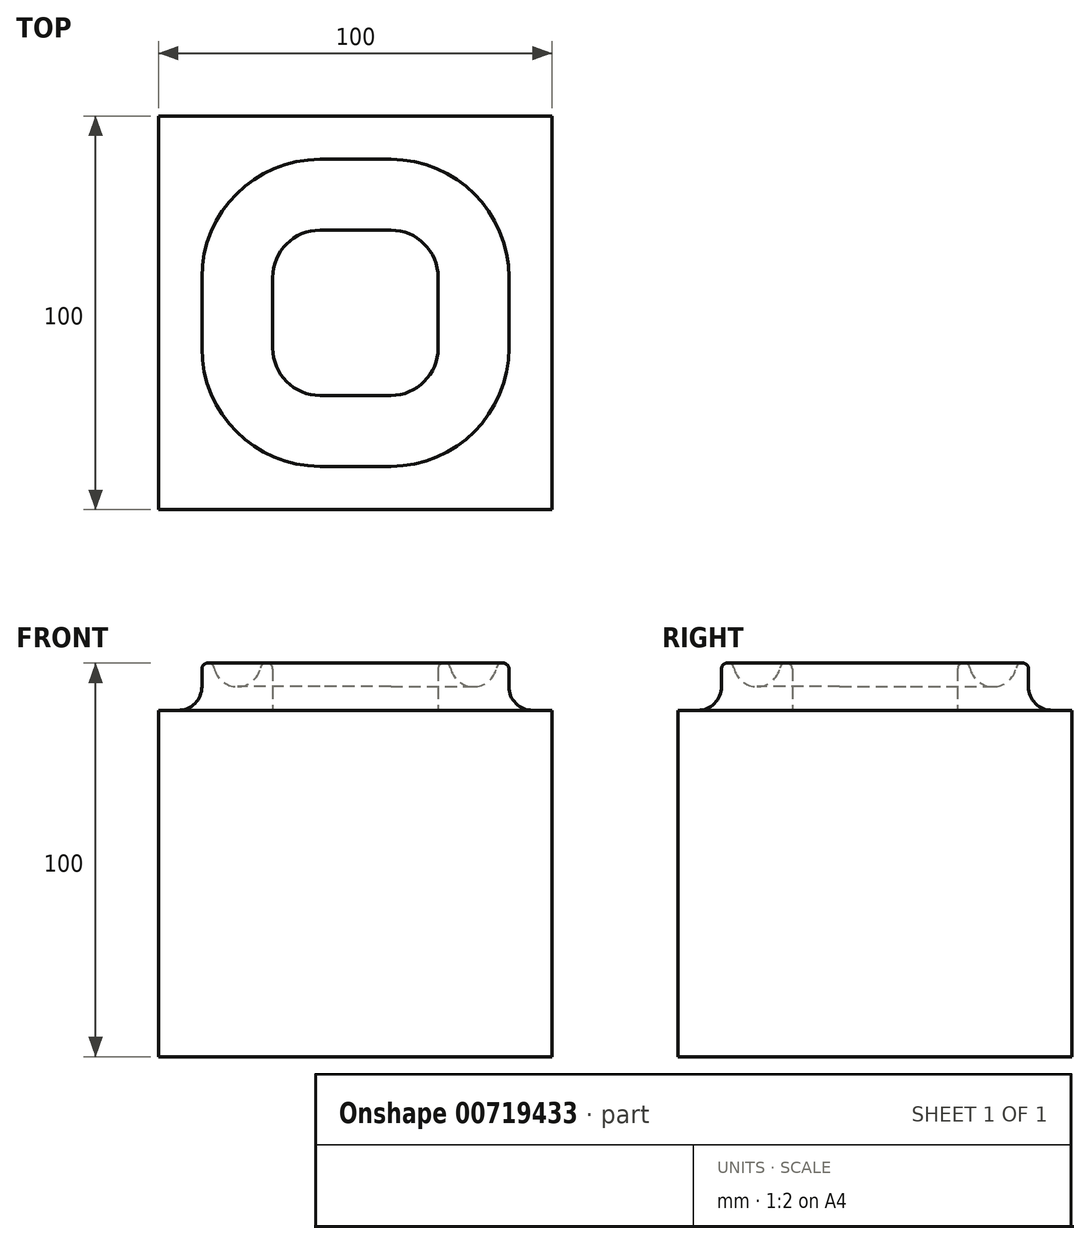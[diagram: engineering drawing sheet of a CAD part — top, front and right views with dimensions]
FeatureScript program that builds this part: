
annotation { "Feature Type Name" : "Feature", "Feature Type Description" : "" }
export const myFeature = defineFeature(function(context is Context, id is Id, definition is map)
    precondition{}
    {
        {
            var Q0;
            Q0=qCreatedBy(makeId("Top.planeOp"),FACE);
            var sketch = newSketch(context, id + "F0", { "sketchPlane" : qUnion([Q0])});
            skLineSegment(sketch, "E0.bottom", {"start": v(50, 50) * mm, "end": v(-50, 50) * mm});
            skLineSegment(sketch, "E0.top", {"start": v(50, -50) * mm, "end": v(-50, -50) * mm});
            skLineSegment(sketch, "E0.left", {"start": v(50, 50) * mm, "end": v(50, -50) * mm});
            skLineSegment(sketch, "E0.right", {"start": v(-50, 50) * mm, "end": v(-50, -50) * mm});
            skPoint(sketch, "E0.middle", {"position": v(0, 0) * mm});
            skLineSegment(sketch, "E1.bottom", {"start": v(9, 15) * mm, "end": v(-9, 15) * mm, "construction": true});
            skLineSegment(sketch, "E1.top", {"start": v(9, -15) * mm, "end": v(-9, -15) * mm, "construction": true});
            skLineSegment(sketch, "E1.left", {"start": v(15, 9) * mm, "end": v(15, -9) * mm, "construction": true});
            skLineSegment(sketch, "E1.right", {"start": v(-15, 9) * mm, "end": v(-15, -9) * mm, "construction": true});
            skPoint(sketch, "E2.visualSharp", {"position": v(-15, 15) * mm});
            skArc(sketch, "E2.filletArc", {"start": v(-9, 15) * mm, "mid": v(-13.24, 13.24) * mm, "end": v(-15, 9) * mm, "construction": true});
            skPoint(sketch, "E3.visualSharp", {"position": v(15, 15) * mm});
            skArc(sketch, "E3.filletArc", {"start": v(15, 9) * mm, "mid": v(13.24, 13.24) * mm, "end": v(9, 15) * mm, "construction": true});
            skPoint(sketch, "E4.visualSharp", {"position": v(15, -15) * mm});
            skArc(sketch, "E4.filletArc", {"start": v(9, -15) * mm, "mid": v(13.24, -13.24) * mm, "end": v(15, -9) * mm, "construction": true});
            skPoint(sketch, "E5.visualSharp", {"position": v(-15, -15) * mm});
            skArc(sketch, "E5.filletArc", {"start": v(-15, -9) * mm, "mid": v(-13.24, -13.24) * mm, "end": v(-9, -15) * mm, "construction": true});
            skArc(sketch, "E6.0", {"start": v(45, 9) * mm, "mid": v(34.46, 34.46) * mm, "end": v(9, 45) * mm, "construction": true});
            skLineSegment(sketch, "E6.1", {"start": v(45, 9) * mm, "end": v(45, -9) * mm, "construction": true});
            skLineSegment(sketch, "E6.2", {"start": v(9, 45) * mm, "end": v(-9, 45) * mm, "construction": true});
            skArc(sketch, "E6.3", {"start": v(9, -45) * mm, "mid": v(34.46, -34.46) * mm, "end": v(45, -9) * mm, "construction": true});
            skArc(sketch, "E6.4", {"start": v(-9, 45) * mm, "mid": v(-34.46, 34.46) * mm, "end": v(-45, 9) * mm, "construction": true});
            skLineSegment(sketch, "E6.5", {"start": v(-45, 9) * mm, "end": v(-45, -9) * mm, "construction": true});
            skArc(sketch, "E6.6", {"start": v(-45, -9) * mm, "mid": v(-34.46, -34.46) * mm, "end": v(-9, -45) * mm, "construction": true});
            skLineSegment(sketch, "E6.7", {"start": v(9, -45) * mm, "end": v(-9, -45) * mm, "construction": true});
            skArc(sketch, "E7.0", {"start": v(21, 9) * mm, "mid": v(17.49, 17.49) * mm, "end": v(9, 21) * mm});
            skLineSegment(sketch, "E7.1", {"start": v(21, 9) * mm, "end": v(21, -9) * mm});
            skLineSegment(sketch, "E7.2", {"start": v(9, 21) * mm, "end": v(-9, 21) * mm});
            skArc(sketch, "E7.3", {"start": v(9, -21) * mm, "mid": v(17.49, -17.49) * mm, "end": v(21, -9) * mm});
            skArc(sketch, "E7.4", {"start": v(-9, 21) * mm, "mid": v(-17.49, 17.49) * mm, "end": v(-21, 9) * mm});
            skLineSegment(sketch, "E7.5", {"start": v(-21, 9) * mm, "end": v(-21, -9) * mm});
            skArc(sketch, "E7.6", {"start": v(-21, -9) * mm, "mid": v(-17.49, -17.49) * mm, "end": v(-9, -21) * mm});
            skLineSegment(sketch, "E7.7", {"start": v(9, -21) * mm, "end": v(-9, -21) * mm});
            skArc(sketch, "E8.0", {"start": v(39, 9) * mm, "mid": v(30.21, 30.21) * mm, "end": v(9, 39) * mm});
            skLineSegment(sketch, "E8.1", {"start": v(39, 9) * mm, "end": v(39, -9) * mm});
            skLineSegment(sketch, "E8.2", {"start": v(9, 39) * mm, "end": v(-9, 39) * mm});
            skArc(sketch, "E8.3", {"start": v(9, -39) * mm, "mid": v(30.21, -30.21) * mm, "end": v(39, -9) * mm});
            skArc(sketch, "E8.4", {"start": v(-9, 39) * mm, "mid": v(-30.21, 30.21) * mm, "end": v(-39, 9) * mm});
            skLineSegment(sketch, "E8.5", {"start": v(-39, 9) * mm, "end": v(-39, -9) * mm});
            skArc(sketch, "E8.6", {"start": v(-39, -9) * mm, "mid": v(-30.21, -30.21) * mm, "end": v(-9, -39) * mm});
            skLineSegment(sketch, "E8.7", {"start": v(9, -39) * mm, "end": v(-9, -39) * mm});
            skArc(sketch, "E9.0", {"start": v(24, 9) * mm, "mid": v(19.6, 19.6) * mm, "end": v(9, 24) * mm});
            skLineSegment(sketch, "E9.1", {"start": v(24, 9) * mm, "end": v(24, -9) * mm});
            skLineSegment(sketch, "E9.2", {"start": v(9, 24) * mm, "end": v(-9, 24) * mm});
            skArc(sketch, "E9.3", {"start": v(9, -24) * mm, "mid": v(19.6, -19.6) * mm, "end": v(24, -9) * mm});
            skArc(sketch, "E9.4", {"start": v(-9, 24) * mm, "mid": v(-19.6, 19.6) * mm, "end": v(-24, 9) * mm});
            skLineSegment(sketch, "E9.5", {"start": v(-24, 9) * mm, "end": v(-24, -9) * mm});
            skArc(sketch, "E9.6", {"start": v(-24, -9) * mm, "mid": v(-19.6, -19.6) * mm, "end": v(-9, -24) * mm});
            skLineSegment(sketch, "E9.7", {"start": v(9, -24) * mm, "end": v(-9, -24) * mm});
            skLineSegment(sketch, "E10.0", {"start": v(9, 36) * mm, "end": v(-9, 36) * mm});
            skArc(sketch, "E10.1", {"start": v(36, 9) * mm, "mid": v(28.1, 28.1) * mm, "end": v(9, 36) * mm});
            skArc(sketch, "E10.2", {"start": v(-9, 36) * mm, "mid": v(-28.1, 28.1) * mm, "end": v(-36, 9) * mm});
            skLineSegment(sketch, "E10.3", {"start": v(36, 9) * mm, "end": v(36, -9) * mm});
            skLineSegment(sketch, "E10.4", {"start": v(-36, 9) * mm, "end": v(-36, -9) * mm});
            skArc(sketch, "E10.5", {"start": v(-36, -9) * mm, "mid": v(-28.1, -28.1) * mm, "end": v(-9, -36) * mm});
            skLineSegment(sketch, "E10.6", {"start": v(9, -36) * mm, "end": v(-9, -36) * mm});
            skArc(sketch, "E10.7", {"start": v(9, -36) * mm, "mid": v(28.1, -28.1) * mm, "end": v(36, -9) * mm});
            skSolve(sketch);
        }
        {
            var Q0;
            Q0=makeQuery(id+"F0.imprint","IMPRINT",FACE,{"disambiguationData":[TD([[makeQuery(id+"F0.imprint","IMPRINT",EDGE,{"derivedFrom":sQuery(id+"F0.wireOp",EDGE,"E0.bottom")}),1.0]])]});
            var Q1;
            Q1=makeQuery(id+"F0.imprint","IMPRINT",FACE,{"disambiguationData":[TD([[makeQuery(id+"F0.imprint","IMPRINT",EDGE,{"derivedFrom":sQuery(id+"F0.wireOp",EDGE,"E9.0")}),-1.0]])]});
            var Q2;
            Q2=makeQuery(id+"F0.imprint","IMPRINT",FACE,{"disambiguationData":[TD([[makeQuery(id+"F0.imprint","IMPRINT",EDGE,{"derivedFrom":sQuery(id+"F0.wireOp",EDGE,"E8.0")}),1.0]])]});
            var Q3;
            Q3=makeQuery(id+"F0.imprint","IMPRINT",FACE,{"disambiguationData":[TD([[makeQuery(id+"F0.imprint","IMPRINT",EDGE,{"derivedFrom":sQuery(id+"F0.wireOp",EDGE,"E7.0")}),-1.0]])]});
            var Q4;
            Q4=makeQuery(id+"F0.imprint","IMPRINT",FACE,{"disambiguationData":[TD([[makeQuery(id+"F0.imprint","IMPRINT",EDGE,{"derivedFrom":sQuery(id+"F0.wireOp",EDGE,"E7.0")}),1.0]])]});
            extrude(context, id + "F1", {"entities" : qUnion([Q0, Q1, Q2, Q3, Q4]), "oppositeDirection" : true, "depth" : 88 * mm, "offsetDistance" : 25 * mm});
        }
        {
            var Q0;
            Q0=makeQuery(id+"F0.imprint","IMPRINT",FACE,{"disambiguationData":[TD([[makeQuery(id+"F0.imprint","IMPRINT",EDGE,{"derivedFrom":sQuery(id+"F0.wireOp",EDGE,"E8.0")}),1.0]])]});
            var Q1;
            Q1=makeQuery(id+"F0.imprint","IMPRINT",FACE,{"disambiguationData":[TD([[makeQuery(id+"F0.imprint","IMPRINT",EDGE,{"derivedFrom":sQuery(id+"F0.wireOp",EDGE,"E9.0")}),-1.0]])]});
            var Q2;
            Q2=makeQuery(id+"F0.imprint","IMPRINT",FACE,{"disambiguationData":[TD([[makeQuery(id+"F0.imprint","IMPRINT",EDGE,{"derivedFrom":sQuery(id+"F0.wireOp",EDGE,"E7.0")}),-1.0]])]});
            extrude(context, id + "F2", {"entities" : qUnion([Q0, Q1, Q2]), "operationType" : NewBodyOperationType.ADD, "depth" : 6 * mm, "offsetDistance" : 25 * mm});
        }
        {
            var Q0;
            Q0=makeQuery(id+"F0.imprint","IMPRINT",FACE,{"disambiguationData":[TD([[makeQuery(id+"F0.imprint","IMPRINT",EDGE,{"derivedFrom":sQuery(id+"F0.wireOp",EDGE,"E8.0")}),1.0]])]});
            var Q1;
            Q1=makeQuery(id+"F0.imprint","IMPRINT",FACE,{"disambiguationData":[TD([[makeQuery(id+"F0.imprint","IMPRINT",EDGE,{"derivedFrom":sQuery(id+"F0.wireOp",EDGE,"E7.0")}),-1.0]])]});
            extrude(context, id + "F3", {"entities" : qUnion([Q0, Q1]), "operationType" : NewBodyOperationType.ADD, "depth" : 12 * mm, "offsetDistance" : 25 * mm});
        }
        {
            var Q0;
            Q0=makeQuery(id+"F2.opExtrude","CAP_EDGE",EDGE,{"disambiguationData":[OSD([sQuery(id+"F0.wireOp",EDGE,"E8.5")])],"isStart":true});
            var Q1;
            Q1=makeQuery(id+"F2.opExtrude","CAP_EDGE",EDGE,{"disambiguationData":[OSD([sQuery(id+"F0.wireOp",EDGE,"E7.4")])],"isStart":true});
            var Q2;
            Q2=makeQuery(id+"F3.boolean.opBoolean","INTERSECT",EDGE,{"derivedFrom":[makeQuery(id+"F2.opExtrude","CAP_FACE",FACE,{"disambiguationData":[OSD([sQuery(id+"F0.wireOp",EDGE,"E7.0"),sQuery(id+"F0.wireOp",EDGE,"E7.1"),sQuery(id+"F0.wireOp",EDGE,"E7.2"),sQuery(id+"F0.wireOp",EDGE,"E7.3"),sQuery(id+"F0.wireOp",EDGE,"E7.4"),sQuery(id+"F0.wireOp",EDGE,"E7.5"),sQuery(id+"F0.wireOp",EDGE,"E7.6"),sQuery(id+"F0.wireOp",EDGE,"E7.7"),sQuery(id+"F0.wireOp",EDGE,"E8.0"),sQuery(id+"F0.wireOp",EDGE,"E8.1"),sQuery(id+"F0.wireOp",EDGE,"E8.2"),sQuery(id+"F0.wireOp",EDGE,"E8.3"),sQuery(id+"F0.wireOp",EDGE,"E8.4"),sQuery(id+"F0.wireOp",EDGE,"E8.5"),sQuery(id+"F0.wireOp",EDGE,"E8.6"),sQuery(id+"F0.wireOp",EDGE,"E8.7")])],"isStart":false}),makeQuery(id+"F3.opExtrude","SWEPT_FACE",FACE,{"disambiguationData":[OSD([sQuery(id+"F0.wireOp",EDGE,"E10.2")])]})]});
            var Q3;
            Q3=makeQuery(id+"F3.boolean.opBoolean","INTERSECT",EDGE,{"derivedFrom":[makeQuery(id+"F2.opExtrude","CAP_FACE",FACE,{"disambiguationData":[OSD([sQuery(id+"F0.wireOp",EDGE,"E7.0"),sQuery(id+"F0.wireOp",EDGE,"E7.1"),sQuery(id+"F0.wireOp",EDGE,"E7.2"),sQuery(id+"F0.wireOp",EDGE,"E7.3"),sQuery(id+"F0.wireOp",EDGE,"E7.4"),sQuery(id+"F0.wireOp",EDGE,"E7.5"),sQuery(id+"F0.wireOp",EDGE,"E7.6"),sQuery(id+"F0.wireOp",EDGE,"E7.7"),sQuery(id+"F0.wireOp",EDGE,"E8.0"),sQuery(id+"F0.wireOp",EDGE,"E8.1"),sQuery(id+"F0.wireOp",EDGE,"E8.2"),sQuery(id+"F0.wireOp",EDGE,"E8.3"),sQuery(id+"F0.wireOp",EDGE,"E8.4"),sQuery(id+"F0.wireOp",EDGE,"E8.5"),sQuery(id+"F0.wireOp",EDGE,"E8.6"),sQuery(id+"F0.wireOp",EDGE,"E8.7")])],"isStart":false}),makeQuery(id+"F3.opExtrude","SWEPT_FACE",FACE,{"disambiguationData":[OSD([sQuery(id+"F0.wireOp",EDGE,"E9.5")])]})]});
            fillet(context, id + "F4", {"entities" : qUnion([Q0, Q1, Q2, Q3]), "radius" : 6 * mm, "tangentPropagation" : true, "allowEdgeOverflow" : false});
        }
        {
            var Q0;
            {var subQ0=sQuery(id+"F0.wireOp",EDGE,"E10.2");var subQ1=sQuery(id+"F0.wireOp",EDGE,"E8.7");var subQ2=sQuery(id+"F0.wireOp",EDGE,"E8.6");var subQ3=sQuery(id+"F0.wireOp",EDGE,"E8.5");var subQ4=sQuery(id+"F0.wireOp",EDGE,"E8.4");var subQ5=sQuery(id+"F0.wireOp",EDGE,"E8.3");var subQ6=sQuery(id+"F0.wireOp",EDGE,"E8.2");var subQ7=sQuery(id+"F0.wireOp",EDGE,"E8.1");var subQ8=sQuery(id+"F0.wireOp",EDGE,"E8.0");Q0=makeQuery(id+"F4.opFillet","BLEND_EDGE",EDGE,{"blendedFrom":[makeQuery(id+"F3.boolean.opBoolean","INTERSECT",EDGE,{"derivedFrom":[makeQuery(id+"F2.opExtrude","CAP_FACE",FACE,{"disambiguationData":[OSD([sQuery(id+"F0.wireOp",EDGE,"E7.0"),sQuery(id+"F0.wireOp",EDGE,"E7.1"),sQuery(id+"F0.wireOp",EDGE,"E7.2"),sQuery(id+"F0.wireOp",EDGE,"E7.3"),sQuery(id+"F0.wireOp",EDGE,"E7.4"),sQuery(id+"F0.wireOp",EDGE,"E7.5"),sQuery(id+"F0.wireOp",EDGE,"E7.6"),sQuery(id+"F0.wireOp",EDGE,"E7.7"),subQ8,subQ7,subQ6,subQ5,subQ4,subQ3,subQ2,subQ1])],"isStart":false}),makeQuery(id+"F3.opExtrude","SWEPT_FACE",FACE,{"disambiguationData":[OSD([subQ0])]})]}),makeQuery(id+"F3.opExtrude","CAP_FACE",FACE,{"disambiguationData":[OSD([subQ8,subQ7,subQ6,subQ5,subQ4,subQ3,subQ2,subQ1,sQuery(id+"F0.wireOp",EDGE,"E10.0"),sQuery(id+"F0.wireOp",EDGE,"E10.1"),subQ0,sQuery(id+"F0.wireOp",EDGE,"E10.3"),sQuery(id+"F0.wireOp",EDGE,"E10.4"),sQuery(id+"F0.wireOp",EDGE,"E10.5"),sQuery(id+"F0.wireOp",EDGE,"E10.6"),sQuery(id+"F0.wireOp",EDGE,"E10.7")])],"isStart":false})],"blendedInto":[makeQuery(id+"F3.opExtrude","CAP_FACE",FACE,{"disambiguationData":[OSD([subQ8,subQ7,subQ6,subQ5,subQ4,subQ3,subQ2,subQ1,sQuery(id+"F0.wireOp",EDGE,"E10.0"),sQuery(id+"F0.wireOp",EDGE,"E10.1"),subQ0,sQuery(id+"F0.wireOp",EDGE,"E10.3"),sQuery(id+"F0.wireOp",EDGE,"E10.4"),sQuery(id+"F0.wireOp",EDGE,"E10.5"),sQuery(id+"F0.wireOp",EDGE,"E10.6"),sQuery(id+"F0.wireOp",EDGE,"E10.7")])],"isStart":false})]});}
            var Q1;
            Q1=makeQuery(id+"F3.opExtrude","CAP_EDGE",EDGE,{"disambiguationData":[OSD([sQuery(id+"F0.wireOp",EDGE,"E8.4")])],"isStart":false});
            var Q2;
            {var subQ0=sQuery(id+"F0.wireOp",EDGE,"E9.5");var subQ1=sQuery(id+"F0.wireOp",EDGE,"E7.7");var subQ2=sQuery(id+"F0.wireOp",EDGE,"E7.6");var subQ3=sQuery(id+"F0.wireOp",EDGE,"E7.5");var subQ4=sQuery(id+"F0.wireOp",EDGE,"E7.4");var subQ5=sQuery(id+"F0.wireOp",EDGE,"E7.3");var subQ6=sQuery(id+"F0.wireOp",EDGE,"E7.2");var subQ7=sQuery(id+"F0.wireOp",EDGE,"E7.1");var subQ8=sQuery(id+"F0.wireOp",EDGE,"E7.0");Q2=makeQuery(id+"F4.opFillet","BLEND_EDGE",EDGE,{"blendedFrom":[makeQuery(id+"F3.boolean.opBoolean","INTERSECT",EDGE,{"derivedFrom":[makeQuery(id+"F2.opExtrude","CAP_FACE",FACE,{"disambiguationData":[OSD([subQ8,subQ7,subQ6,subQ5,subQ4,subQ3,subQ2,subQ1,sQuery(id+"F0.wireOp",EDGE,"E8.0"),sQuery(id+"F0.wireOp",EDGE,"E8.1"),sQuery(id+"F0.wireOp",EDGE,"E8.2"),sQuery(id+"F0.wireOp",EDGE,"E8.3"),sQuery(id+"F0.wireOp",EDGE,"E8.4"),sQuery(id+"F0.wireOp",EDGE,"E8.5"),sQuery(id+"F0.wireOp",EDGE,"E8.6"),sQuery(id+"F0.wireOp",EDGE,"E8.7")])],"isStart":false}),makeQuery(id+"F3.opExtrude","SWEPT_FACE",FACE,{"disambiguationData":[OSD([subQ0])]})]}),makeQuery(id+"F3.opExtrude","CAP_FACE",FACE,{"disambiguationData":[OSD([subQ8,subQ7,subQ6,subQ5,subQ4,subQ3,subQ2,subQ1,sQuery(id+"F0.wireOp",EDGE,"E9.0"),sQuery(id+"F0.wireOp",EDGE,"E9.1"),sQuery(id+"F0.wireOp",EDGE,"E9.2"),sQuery(id+"F0.wireOp",EDGE,"E9.3"),sQuery(id+"F0.wireOp",EDGE,"E9.4"),subQ0,sQuery(id+"F0.wireOp",EDGE,"E9.6"),sQuery(id+"F0.wireOp",EDGE,"E9.7")])],"isStart":false})],"blendedInto":[makeQuery(id+"F3.opExtrude","CAP_FACE",FACE,{"disambiguationData":[OSD([subQ8,subQ7,subQ6,subQ5,subQ4,subQ3,subQ2,subQ1,sQuery(id+"F0.wireOp",EDGE,"E9.0"),sQuery(id+"F0.wireOp",EDGE,"E9.1"),sQuery(id+"F0.wireOp",EDGE,"E9.2"),sQuery(id+"F0.wireOp",EDGE,"E9.3"),sQuery(id+"F0.wireOp",EDGE,"E9.4"),subQ0,sQuery(id+"F0.wireOp",EDGE,"E9.6"),sQuery(id+"F0.wireOp",EDGE,"E9.7")])],"isStart":false})]});}
            var Q3;
            Q3=makeQuery(id+"F3.opExtrude","CAP_EDGE",EDGE,{"disambiguationData":[OSD([sQuery(id+"F0.wireOp",EDGE,"E7.5")])],"isStart":false});
            fillet(context, id + "F5", {"entities" : qUnion([Q0, Q1, Q2, Q3]), "radius" : 1.5 * mm, "tangentPropagation" : true, "allowEdgeOverflow" : false});
        }
    });
